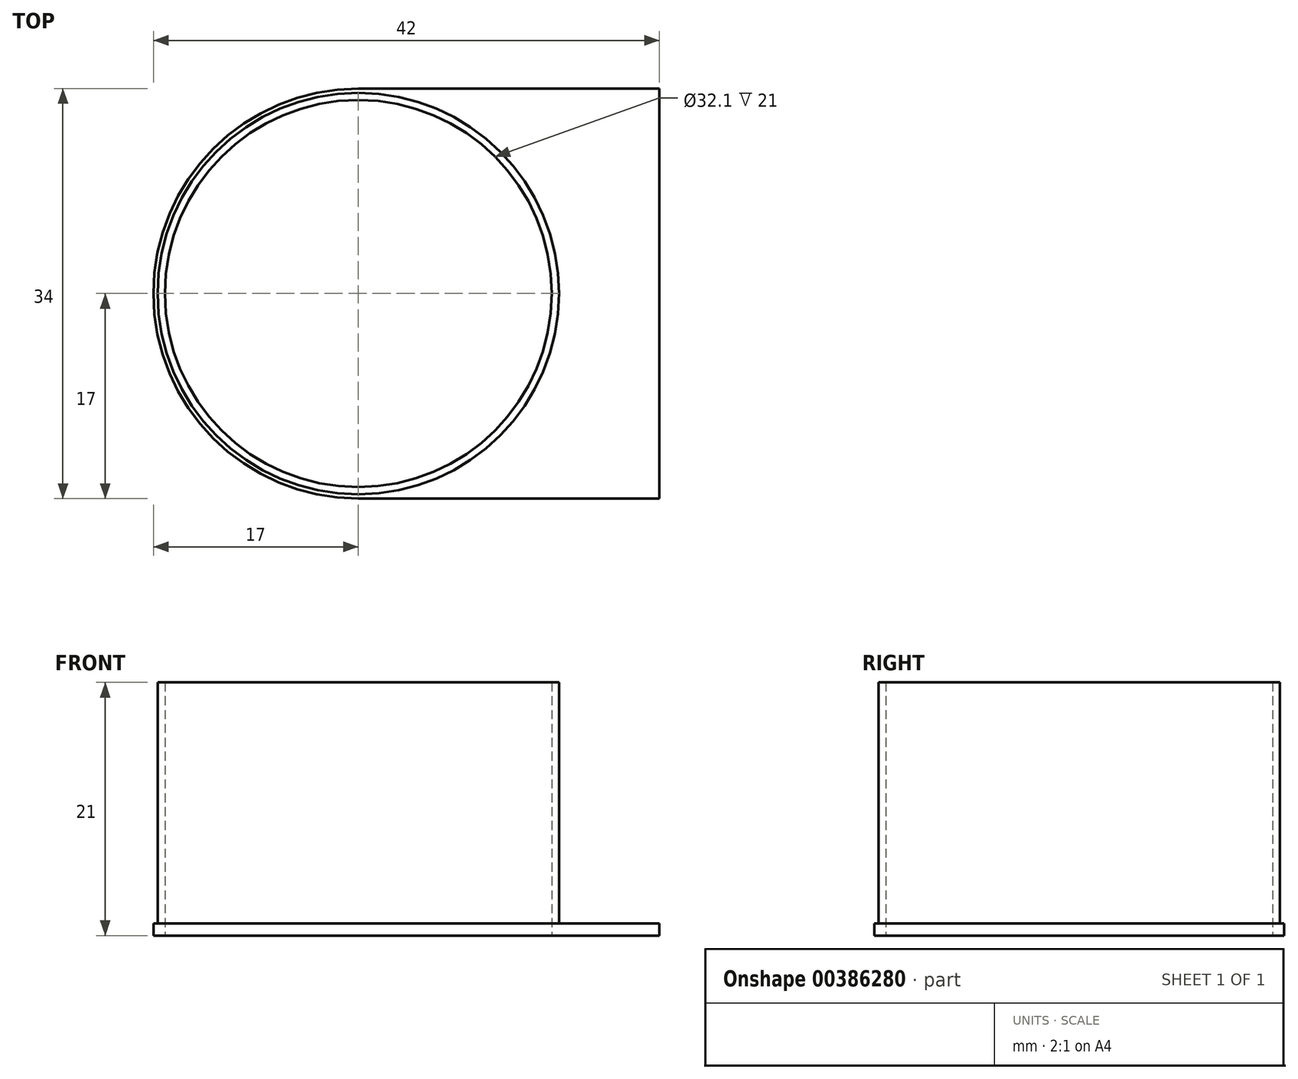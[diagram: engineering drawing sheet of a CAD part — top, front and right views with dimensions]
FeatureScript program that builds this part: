
annotation { "Feature Type Name" : "Feature", "Feature Type Description" : "" }
export const myFeature = defineFeature(function(context is Context, id is Id, definition is map)
    precondition{}
    {
        {
            var Q0;
            Q0=qCreatedBy(makeId("Top.planeOp"),FACE);
            var sketch = newSketch(context, id + "F0", { "sketchPlane" : qUnion([Q0])});
            skCircle(sketch, "E0", {"center": v(0, 0) * mm, "radius": 16.05 * mm});
            skCircle(sketch, "E1.0", {"center": v(0, 0) * mm, "radius": 17 * mm});
            skLineSegment(sketch, "E2", {"start": v(0, 17) * mm, "end": v(25, 17) * mm});
            skLineSegment(sketch, "E3", {"start": v(25, 17) * mm, "end": v(25, -17) * mm});
            skLineSegment(sketch, "E4", {"start": v(0, -17) * mm, "end": v(25, -17) * mm});
            skSolve(sketch);
        }
        {
            var Q0;
            Q0 = qSketchRegion(id + "F0", true);
            extrude(context, id + "F1", {"entities" : qUnion([Q0]), "depth" : 1 * mm});
        }
        {
            var Q0;
            Q0=makeQuery(id+"F1.opExtrude","CAP_FACE",FACE,{"disambiguationData":[OSD([sQuery(id+"F0.wireOp",EDGE,"E0"),sQuery(id+"F0.wireOp",EDGE,"E1.0")])],"isStart":false});
            var sketch = newSketch(context, id + "F2", { "sketchPlane" : qUnion([Q0])});
            skCircle(sketch, "E5.0", {"center": v(0, 0) * mm, "radius": 16.05 * mm});
            skCircle(sketch, "E6.0", {"center": v(0, 0) * mm, "radius": 16.65 * mm});
            skSolve(sketch);
        }
        {
            var Q0;
            Q0 = qSketchRegion(id + "F2", true);
            extrude(context, id + "F3", {"entities" : qUnion([Q0]), "operationType" : NewBodyOperationType.ADD, "depth" : 20 * mm});
        }
    });
